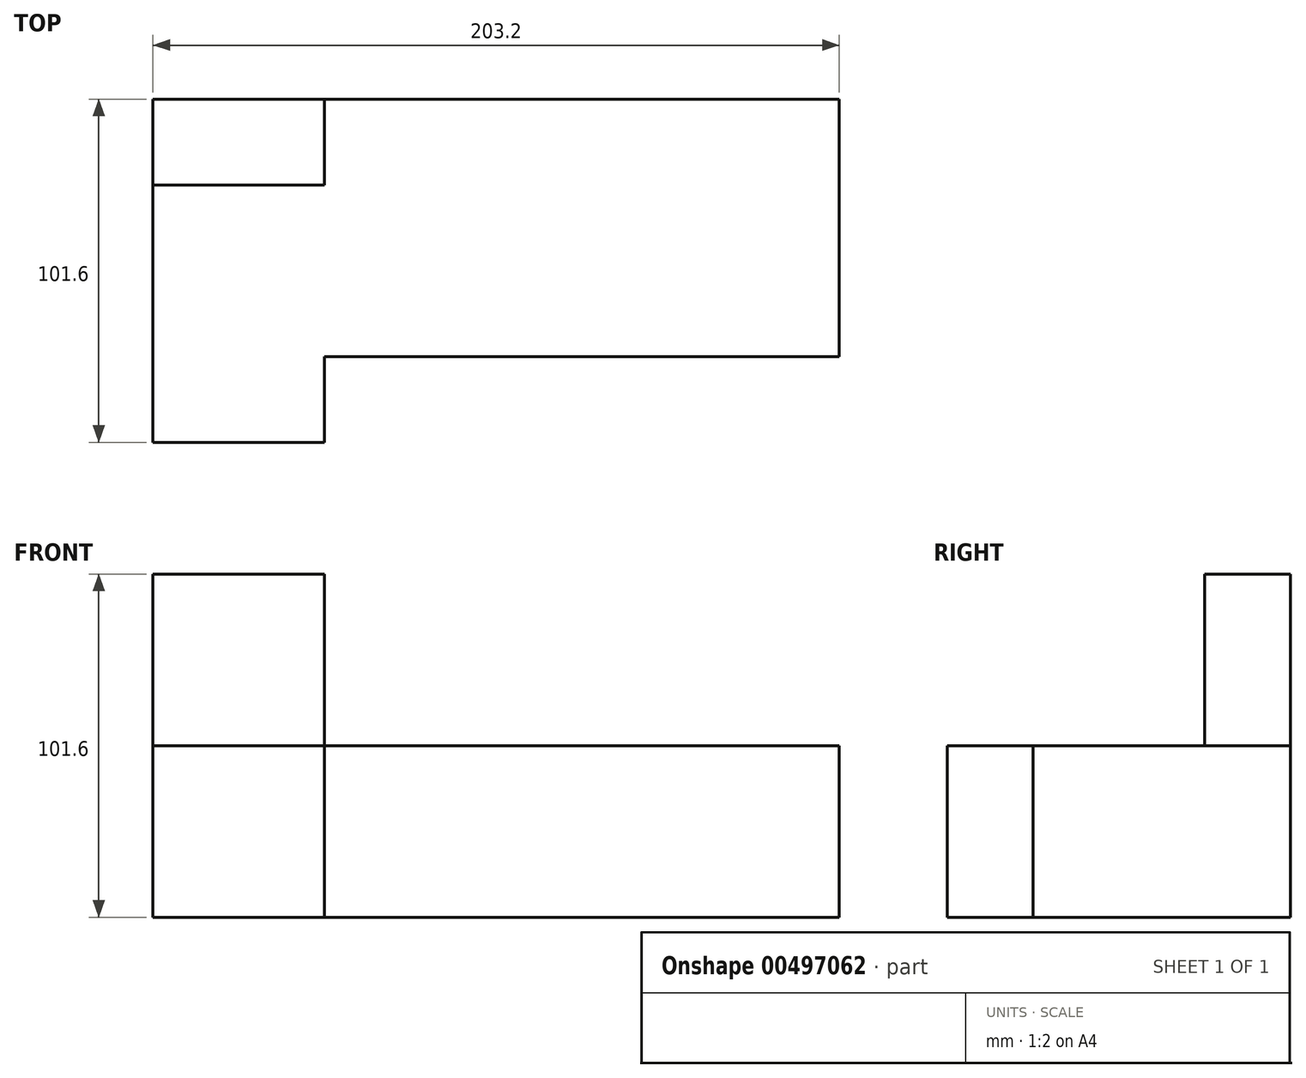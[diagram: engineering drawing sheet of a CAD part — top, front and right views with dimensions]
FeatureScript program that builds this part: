
annotation { "Feature Type Name" : "Feature", "Feature Type Description" : "" }
export const myFeature = defineFeature(function(context is Context, id is Id, definition is map)
    precondition{}
    {
        {
            var Q0;
            Q0=qCreatedBy(makeId("Top.planeOp"),FACE);
            var sketch = newSketch(context, id + "F0", { "sketchPlane" : qUnion([Q0])});
            skLineSegment(sketch, "E0.bottom", {"start": v(0, 0) * mm, "end": v(203.2, 0) * mm});
            skLineSegment(sketch, "E0.top", {"start": v(0, 76.2) * mm, "end": v(203.2, 76.2) * mm});
            skLineSegment(sketch, "E0.left", {"start": v(0, 0) * mm, "end": v(0, 76.2) * mm});
            skLineSegment(sketch, "E0.right", {"start": v(203.2, 0) * mm, "end": v(203.2, 76.2) * mm});
            skSolve(sketch);
        }
        {
            var Q0;
            Q0 = qSketchRegion(id + "F0", true);
            extrude(context, id + "F1", {"entities" : qUnion([Q0]), "depth" : 50.8 * mm});
        }
        {
            var Q0;
            Q0=makeQuery(id+"F1.opExtrude","CAP_FACE",FACE,{"disambiguationData":[OSD([sQuery(id+"F0.wireOp",EDGE,"E0.bottom"),sQuery(id+"F0.wireOp",EDGE,"E0.top"),sQuery(id+"F0.wireOp",EDGE,"E0.left"),sQuery(id+"F0.wireOp",EDGE,"E0.right")])],"isStart":false});
            var sketch = newSketch(context, id + "F2", { "sketchPlane" : qUnion([Q0])});
            skLineSegment(sketch, "E1.bottom", {"start": v(0, 76.2) * mm, "end": v(50.8, 76.2) * mm});
            skLineSegment(sketch, "E1.top", {"start": v(0, 50.8) * mm, "end": v(50.8, 50.8) * mm});
            skLineSegment(sketch, "E1.left", {"start": v(0, 76.2) * mm, "end": v(0, 50.8) * mm});
            skLineSegment(sketch, "E1.right", {"start": v(50.8, 76.2) * mm, "end": v(50.8, 50.8) * mm});
            skSolve(sketch);
        }
        {
            var Q0;
            Q0 = qSketchRegion(id + "F2", true);
            extrude(context, id + "F3", {"entities" : qUnion([Q0]), "operationType" : NewBodyOperationType.ADD, "depth" : 50.8 * mm});
        }
        {
            var Q0;
            Q0=makeQuery(id+"F1.opExtrude","SWEPT_FACE",FACE,{"disambiguationData":[OSD([sQuery(id+"F0.wireOp",EDGE,"E0.bottom")])]});
            var sketch = newSketch(context, id + "F4", { "sketchPlane" : qUnion([Q0])});
            skLineSegment(sketch, "E2.bottom", {"start": v(0, 0) * mm, "end": v(50.8, 0) * mm});
            skLineSegment(sketch, "E2.top", {"start": v(0, 50.8) * mm, "end": v(50.8, 50.8) * mm});
            skLineSegment(sketch, "E2.left", {"start": v(0, 0) * mm, "end": v(0, 50.8) * mm});
            skLineSegment(sketch, "E2.right", {"start": v(50.8, 0) * mm, "end": v(50.8, 50.8) * mm});
            skSolve(sketch);
        }
        {
            var Q0;
            Q0 = qSketchRegion(id + "F4", true);
            extrude(context, id + "F5", {"entities" : qUnion([Q0]), "operationType" : NewBodyOperationType.ADD, "depth" : 25.4 * mm});
        }
    });
